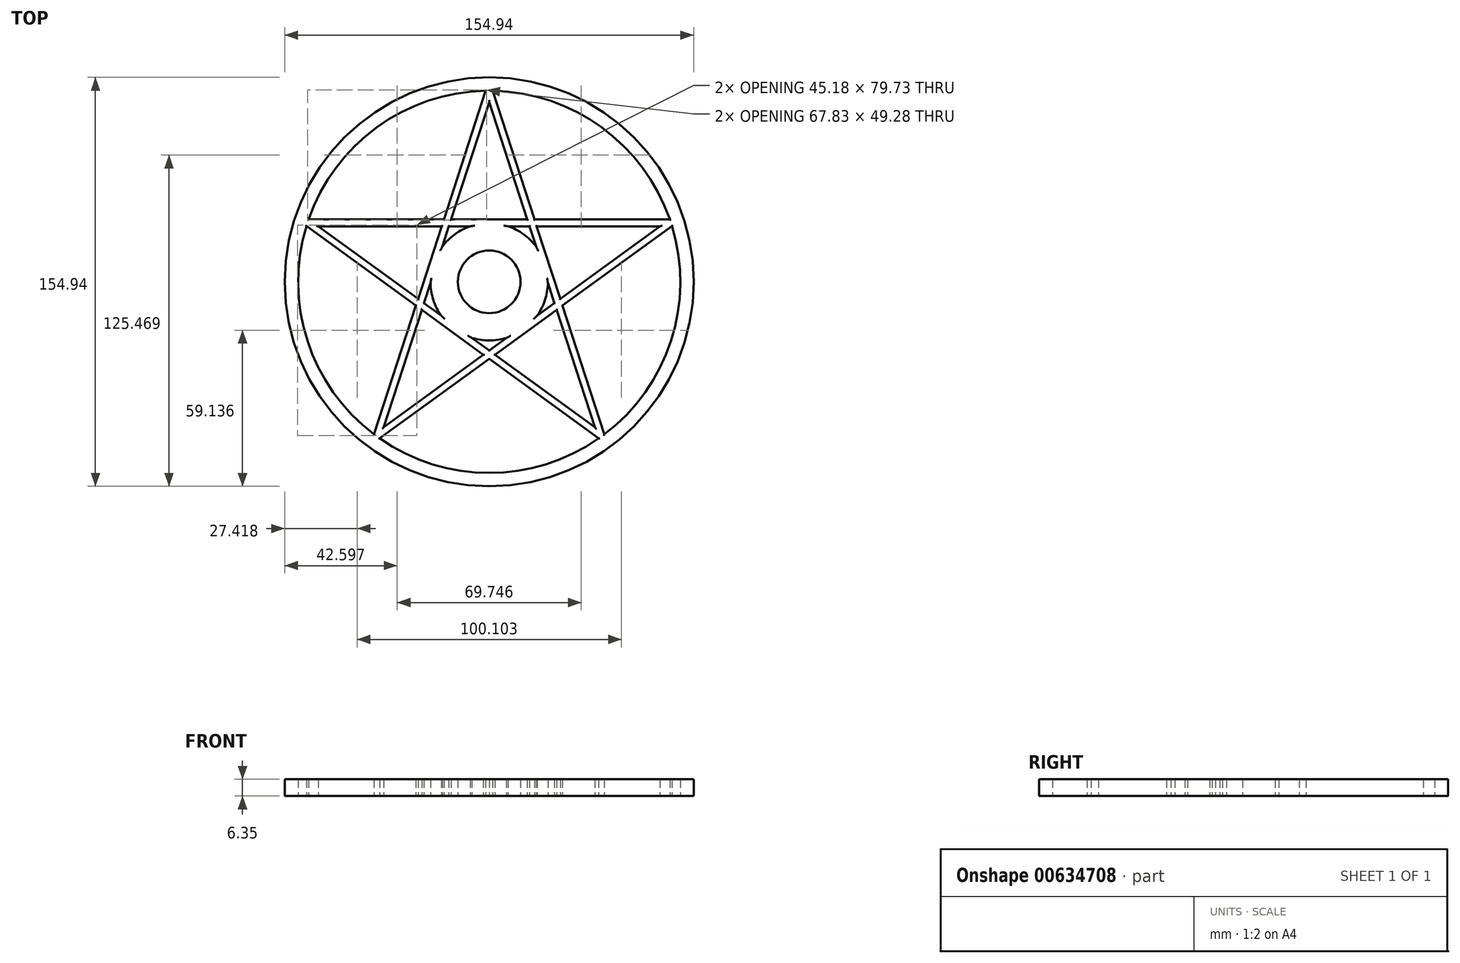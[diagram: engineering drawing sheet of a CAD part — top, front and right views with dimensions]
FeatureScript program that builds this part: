
annotation { "Feature Type Name" : "Feature", "Feature Type Description" : "" }
export const myFeature = defineFeature(function(context is Context, id is Id, definition is map)
    precondition{}
    {
        {
            var Q0;
            Q0=qCreatedBy(makeId("Top.planeOp"),FACE);
            var sketch = newSketch(context, id + "F0", { "sketchPlane" : qUnion([Q0])});
            skPoint(sketch, "E0.center", {"position": v(0, 0) * mm});
            skLineSegment(sketch, "E1", {"start": v(0, 76.42) * mm, "end": v(-17.16, 23.61) * mm});
            skLineSegment(sketch, "E2", {"start": v(-44.92, -61.82) * mm, "end": v(0, -29.19) * mm});
            skLineSegment(sketch, "E3", {"start": v(72.68, 23.61) * mm, "end": v(17.16, 23.61) * mm});
            skLineSegment(sketch, "E4", {"start": v(-72.68, 23.61) * mm, "end": v(-27.76, -9.02) * mm});
            skLineSegment(sketch, "E5", {"start": v(44.92, -61.82) * mm, "end": v(27.76, -9.02) * mm});
            skLineSegment(sketch, "E6", {"start": v(0, 68.05) * mm, "end": v(-14.44, 23.61) * mm});
            skLineSegment(sketch, "E7", {"start": v(-40, -55.06) * mm, "end": v(-2.2, -27.6) * mm});
            skLineSegment(sketch, "E8", {"start": v(64.72, 21.03) * mm, "end": v(18, 21.03) * mm});
            skLineSegment(sketch, "E9", {"start": v(-64.72, 21.03) * mm, "end": v(-26.92, -6.44) * mm});
            skLineSegment(sketch, "E10", {"start": v(40, -55.06) * mm, "end": v(25.56, -10.62) * mm});
            skLineSegment(sketch, "E11.trimOffspring", {"start": v(-18, 21.03) * mm, "end": v(-26.92, -6.44) * mm});
            skLineSegment(sketch, "E12.trimOffspring", {"start": v(-17.16, 23.61) * mm, "end": v(-72.68, 23.61) * mm});
            skLineSegment(sketch, "E13.trimOffspring", {"start": v(-15.28, 21.03) * mm, "end": v(-24.72, -8.03) * mm});
            skLineSegment(sketch, "E14.trimOffspring", {"start": v(-18, 21.03) * mm, "end": v(-64.72, 21.03) * mm});
            skLineSegment(sketch, "E15.trimOffspring", {"start": v(14.44, 23.61) * mm, "end": v(0, 68.05) * mm});
            skLineSegment(sketch, "E16.trimOffspring", {"start": v(14.44, 23.61) * mm, "end": v(-14.44, 23.61) * mm});
            skLineSegment(sketch, "E17.trimOffspring", {"start": v(17.16, 23.61) * mm, "end": v(0, 76.42) * mm});
            skLineSegment(sketch, "E18.trimOffspring", {"start": v(15.28, 21.03) * mm, "end": v(-15.28, 21.03) * mm});
            skLineSegment(sketch, "E19.trimOffspring", {"start": v(26.92, -6.44) * mm, "end": v(18, 21.03) * mm});
            skLineSegment(sketch, "E20.trimOffspring", {"start": v(26.92, -6.44) * mm, "end": v(64.72, 21.03) * mm});
            skLineSegment(sketch, "E21.trimOffspring", {"start": v(24.72, -8.03) * mm, "end": v(15.28, 21.03) * mm});
            skLineSegment(sketch, "E22.trimOffspring", {"start": v(27.76, -9.02) * mm, "end": v(72.68, 23.61) * mm});
            skLineSegment(sketch, "E23.trimOffspring", {"start": v(2.2, -27.6) * mm, "end": v(40, -55.06) * mm});
            skLineSegment(sketch, "E24.trimOffspring", {"start": v(0, -26) * mm, "end": v(24.72, -8.03) * mm});
            skLineSegment(sketch, "E25.trimOffspring", {"start": v(0, -29.19) * mm, "end": v(44.92, -61.82) * mm});
            skLineSegment(sketch, "E26.trimOffspring", {"start": v(2.2, -27.6) * mm, "end": v(25.56, -10.62) * mm});
            skLineSegment(sketch, "E27.trimOffspring", {"start": v(-27.76, -9.02) * mm, "end": v(-44.92, -61.82) * mm});
            skLineSegment(sketch, "E28.trimOffspring", {"start": v(-24.72, -8.03) * mm, "end": v(0, -26) * mm});
            skLineSegment(sketch, "E29.trimOffspring", {"start": v(-25.56, -10.62) * mm, "end": v(-40, -55.06) * mm});
            skLineSegment(sketch, "E30.trimOffspring", {"start": v(-25.56, -10.62) * mm, "end": v(-2.2, -27.6) * mm});
            skSolve(sketch);
        }
        {
            var Q0;
            Q0=makeQuery(id+"F0.imprint","IMPRINT",FACE,{"disambiguationData":[TD([[makeQuery(id+"F0.imprint","IMPRINT",EDGE,{"derivedFrom":sQuery(id+"F0.wireOp",EDGE,"E1")}),1.0]])]});
            extrude(context, id + "F1", {"entities" : qUnion([Q0]), "depth" : 6.35 * mm, "offsetDistance" : 25.4 * mm});
        }
        {
            var Q0;
            Q0=qCreatedBy(makeId("Top.planeOp"),FACE);
            var sketch = newSketch(context, id + "F2", { "sketchPlane" : qUnion([Q0])});
            skCircle(sketch, "E31", {"center": v(0, 0) * mm, "radius": 77.47 * mm});
            skCircle(sketch, "E32", {"center": v(0, 0) * mm, "radius": 72.4 * mm});
            skSolve(sketch);
        }
        {
            var Q0;
            Q0=makeQuery(id+"F2.imprint","IMPRINT",FACE,{"disambiguationData":[TD([[makeQuery(id+"F2.imprint","IMPRINT",EDGE,{"derivedFrom":sQuery(id+"F2.wireOp",EDGE,"E31")}),1.0]])]});
            extrude(context, id + "F3", {"entities" : qUnion([Q0]), "operationType" : NewBodyOperationType.ADD, "depth" : 6.35 * mm, "offsetDistance" : 25.4 * mm});
        }
        {
            var Q0;
            Q0=qCreatedBy(makeId("Top.planeOp"),FACE);
            var sketch = newSketch(context, id + "F4", { "sketchPlane" : qUnion([Q0])});
            skCircle(sketch, "E33", {"center": v(0, 0) * mm, "radius": 11.87 * mm});
            skCircle(sketch, "E34", {"center": v(0, 0) * mm, "radius": 22.23 * mm});
            skSolve(sketch);
        }
        {
            var Q0;
            Q0=makeQuery(id+"F4.imprint","IMPRINT",FACE,{"disambiguationData":[TD([[makeQuery(id+"F4.imprint","IMPRINT",EDGE,{"derivedFrom":sQuery(id+"F4.wireOp",EDGE,"E33")}),-1.0]])]});
            extrude(context, id + "F5", {"entities" : qUnion([Q0]), "operationType" : NewBodyOperationType.ADD, "depth" : 6.35 * mm, "offsetDistance" : 25.4 * mm});
        }
        {
            var Q0;
            Q0=makeQuery(id+"F5.boolean.opBoolean","MERGE",FACE,{"derivedFrom":[makeQuery(id+"F3.boolean.opBoolean","MERGE",FACE,{"derivedFrom":[makeQuery(id+"F1.opExtrude","CAP_FACE",FACE,{"disambiguationData":[OSD([sQuery(id+"F0.wireOp",EDGE,"E1"),sQuery(id+"F0.wireOp",EDGE,"E2"),sQuery(id+"F0.wireOp",EDGE,"E3"),sQuery(id+"F0.wireOp",EDGE,"E4"),sQuery(id+"F0.wireOp",EDGE,"E5"),sQuery(id+"F0.wireOp",EDGE,"E6"),sQuery(id+"F0.wireOp",EDGE,"E7"),sQuery(id+"F0.wireOp",EDGE,"E8"),sQuery(id+"F0.wireOp",EDGE,"E9"),sQuery(id+"F0.wireOp",EDGE,"E10"),sQuery(id+"F0.wireOp",EDGE,"E11.trimOffspring"),sQuery(id+"F0.wireOp",EDGE,"E12.trimOffspring"),sQuery(id+"F0.wireOp",EDGE,"E13.trimOffspring"),sQuery(id+"F0.wireOp",EDGE,"E14.trimOffspring"),sQuery(id+"F0.wireOp",EDGE,"E15.trimOffspring"),sQuery(id+"F0.wireOp",EDGE,"E16.trimOffspring"),sQuery(id+"F0.wireOp",EDGE,"E17.trimOffspring"),sQuery(id+"F0.wireOp",EDGE,"E18.trimOffspring"),sQuery(id+"F0.wireOp",EDGE,"E19.trimOffspring"),sQuery(id+"F0.wireOp",EDGE,"E20.trimOffspring"),sQuery(id+"F0.wireOp",EDGE,"E21.trimOffspring"),sQuery(id+"F0.wireOp",EDGE,"E22.trimOffspring"),sQuery(id+"F0.wireOp",EDGE,"E23.trimOffspring"),sQuery(id+"F0.wireOp",EDGE,"E24.trimOffspring"),sQuery(id+"F0.wireOp",EDGE,"E25.trimOffspring"),sQuery(id+"F0.wireOp",EDGE,"E26.trimOffspring"),sQuery(id+"F0.wireOp",EDGE,"E27.trimOffspring"),sQuery(id+"F0.wireOp",EDGE,"E28.trimOffspring"),sQuery(id+"F0.wireOp",EDGE,"E29.trimOffspring"),sQuery(id+"F0.wireOp",EDGE,"E30.trimOffspring")])],"isStart":false}),makeQuery(id+"F3.opExtrude","CAP_FACE",FACE,{"disambiguationData":[OSD([sQuery(id+"F2.wireOp",EDGE,"E31"),sQuery(id+"F2.wireOp",EDGE,"E32")])],"isStart":false})]}),makeQuery(id+"F5.opExtrude","CAP_FACE",FACE,{"disambiguationData":[OSD([sQuery(id+"F4.wireOp",EDGE,"E33"),sQuery(id+"F4.wireOp",EDGE,"E34")])],"isStart":false})]});
            var Q1;
            Q1=makeQuery(id+"F5.boolean.opBoolean","MERGE",FACE,{"derivedFrom":[makeQuery(id+"F3.boolean.opBoolean","MERGE",FACE,{"derivedFrom":[makeQuery(id+"F1.opExtrude","CAP_FACE",FACE,{"disambiguationData":[OSD([sQuery(id+"F0.wireOp",EDGE,"E1"),sQuery(id+"F0.wireOp",EDGE,"E2"),sQuery(id+"F0.wireOp",EDGE,"E3"),sQuery(id+"F0.wireOp",EDGE,"E4"),sQuery(id+"F0.wireOp",EDGE,"E5"),sQuery(id+"F0.wireOp",EDGE,"E6"),sQuery(id+"F0.wireOp",EDGE,"E7"),sQuery(id+"F0.wireOp",EDGE,"E8"),sQuery(id+"F0.wireOp",EDGE,"E9"),sQuery(id+"F0.wireOp",EDGE,"E10"),sQuery(id+"F0.wireOp",EDGE,"E11.trimOffspring"),sQuery(id+"F0.wireOp",EDGE,"E12.trimOffspring"),sQuery(id+"F0.wireOp",EDGE,"E13.trimOffspring"),sQuery(id+"F0.wireOp",EDGE,"E14.trimOffspring"),sQuery(id+"F0.wireOp",EDGE,"E15.trimOffspring"),sQuery(id+"F0.wireOp",EDGE,"E16.trimOffspring"),sQuery(id+"F0.wireOp",EDGE,"E17.trimOffspring"),sQuery(id+"F0.wireOp",EDGE,"E18.trimOffspring"),sQuery(id+"F0.wireOp",EDGE,"E19.trimOffspring"),sQuery(id+"F0.wireOp",EDGE,"E20.trimOffspring"),sQuery(id+"F0.wireOp",EDGE,"E21.trimOffspring"),sQuery(id+"F0.wireOp",EDGE,"E22.trimOffspring"),sQuery(id+"F0.wireOp",EDGE,"E23.trimOffspring"),sQuery(id+"F0.wireOp",EDGE,"E24.trimOffspring"),sQuery(id+"F0.wireOp",EDGE,"E25.trimOffspring"),sQuery(id+"F0.wireOp",EDGE,"E26.trimOffspring"),sQuery(id+"F0.wireOp",EDGE,"E27.trimOffspring"),sQuery(id+"F0.wireOp",EDGE,"E28.trimOffspring"),sQuery(id+"F0.wireOp",EDGE,"E29.trimOffspring"),sQuery(id+"F0.wireOp",EDGE,"E30.trimOffspring")])],"isStart":true}),makeQuery(id+"F3.opExtrude","CAP_FACE",FACE,{"disambiguationData":[OSD([sQuery(id+"F2.wireOp",EDGE,"E31"),sQuery(id+"F2.wireOp",EDGE,"E32")])],"isStart":true})]}),makeQuery(id+"F5.opExtrude","CAP_FACE",FACE,{"disambiguationData":[OSD([sQuery(id+"F4.wireOp",EDGE,"E33"),sQuery(id+"F4.wireOp",EDGE,"E34")])],"isStart":true})]});
            fillet(context, id + "F6", {"entities" : qUnion([Q0, Q1]), "radius" : 0.25 * mm, "tangentPropagation" : true, "allowEdgeOverflow" : false});
        }
    });
